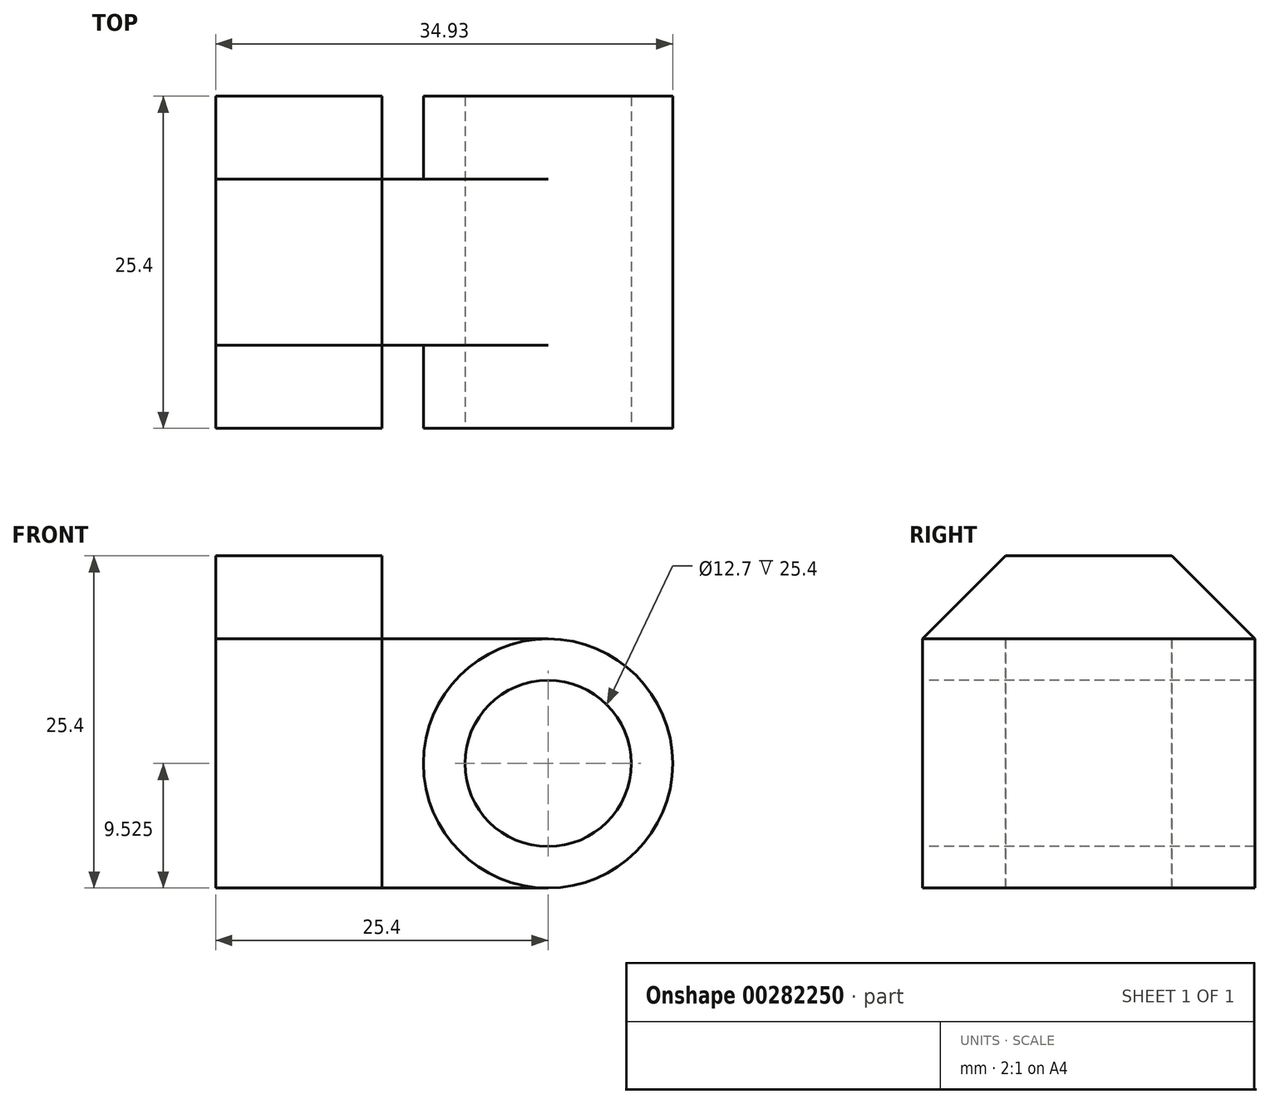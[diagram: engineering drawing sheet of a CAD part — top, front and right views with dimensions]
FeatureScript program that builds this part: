
annotation { "Feature Type Name" : "Feature", "Feature Type Description" : "" }
export const myFeature = defineFeature(function(context is Context, id is Id, definition is map)
    precondition{}
    {
        {
            var Q0;
            Q0=qCreatedBy(makeId("Right.planeOp"),FACE);
            var sketch = newSketch(context, id + "F0", { "sketchPlane" : qUnion([Q0])});
            skLineSegment(sketch, "E0.bottom", {"start": v(0, 0) * mm, "end": v(25.4, 0) * mm});
            skLineSegment(sketch, "E0.top", {"start": v(0, 25.4) * mm, "end": v(25.4, 25.4) * mm});
            skLineSegment(sketch, "E0.left", {"start": v(0, 0) * mm, "end": v(0, 25.4) * mm});
            skLineSegment(sketch, "E0.right", {"start": v(25.4, 0) * mm, "end": v(25.4, 25.4) * mm});
            skSolve(sketch);
        }
        {
            var Q0;
            Q0 = qSketchRegion(id + "F0", true);
            extrude(context, id + "F1", {"entities" : qUnion([Q0]), "depth" : 12.7 * mm});
        }
        {
            var Q0;
            Q0=qCreatedBy(makeId("Right.planeOp"),FACE);
            var sketch = newSketch(context, id + "F2", { "sketchPlane" : qUnion([Q0])});
            skLineSegment(sketch, "E1", {"start": v(0, 25.4) * mm, "end": v(0, 19.05) * mm});
            skLineSegment(sketch, "E2", {"start": v(0, 25.4) * mm, "end": v(6.35, 25.4) * mm});
            skLineSegment(sketch, "E3", {"start": v(6.35, 25.4) * mm, "end": v(0, 19.05) * mm});
            skSolve(sketch);
        }
        {
            var Q0;
            Q0 = qSketchRegion(id + "F2", true);
            extrude(context, id + "F3", {"entities" : qUnion([Q0]), "operationType" : NewBodyOperationType.REMOVE, "depth" : 12.7 * mm});
        }
        {
            var Q0;
            Q0=qCreatedBy(makeId("Right.planeOp"),FACE);
            var sketch = newSketch(context, id + "F4", { "sketchPlane" : qUnion([Q0])});
            skLineSegment(sketch, "E4", {"start": v(25.4, 19.05) * mm, "end": v(25.4, 25.4) * mm});
            skLineSegment(sketch, "E5", {"start": v(25.4, 25.4) * mm, "end": v(19.05, 25.4) * mm});
            skLineSegment(sketch, "E6", {"start": v(19.05, 25.4) * mm, "end": v(25.4, 19.05) * mm});
            skSolve(sketch);
        }
        {
            var Q0;
            Q0 = qSketchRegion(id + "F4", true);
            extrude(context, id + "F5", {"entities" : qUnion([Q0]), "operationType" : NewBodyOperationType.REMOVE, "depth" : 12.7 * mm});
        }
        {
            var Q0;
            Q0=makeQuery(id+"F1.opExtrude","CAP_FACE",FACE,{"disambiguationData":[OSD([sQuery(id+"F0.wireOp",EDGE,"E0.bottom"),sQuery(id+"F0.wireOp",EDGE,"E0.top"),sQuery(id+"F0.wireOp",EDGE,"E0.left"),sQuery(id+"F0.wireOp",EDGE,"E0.right")])],"isStart":false});
            var sketch = newSketch(context, id + "F6", { "sketchPlane" : qUnion([Q0])});
            skLineSegment(sketch, "E7.bottom", {"start": v(6.35, 19.05) * mm, "end": v(19.05, 19.05) * mm});
            skLineSegment(sketch, "E7.top", {"start": v(6.35, 0) * mm, "end": v(19.05, 0) * mm});
            skLineSegment(sketch, "E7.left", {"start": v(6.35, 19.05) * mm, "end": v(6.35, 0) * mm});
            skLineSegment(sketch, "E7.right", {"start": v(19.05, 19.05) * mm, "end": v(19.05, 0) * mm});
            skSolve(sketch);
        }
        {
            var Q0;
            Q0 = qSketchRegion(id + "F6", true);
            extrude(context, id + "F7", {"entities" : qUnion([Q0]), "operationType" : NewBodyOperationType.ADD, "depth" : 12.7 * mm});
        }
        {
            var Q0;
            Q0=qCreatedBy(makeId("Front.planeOp"),FACE);
            var sketch = newSketch(context, id + "F8", { "sketchPlane" : qUnion([Q0])});
            skCircle(sketch, "E8", {"center": v(25.4, 9.53) * mm, "radius": 9.53 * mm});
            skSolve(sketch);
        }
        {
            var Q0;
            Q0 = qSketchRegion(id + "F8", true);
            extrude(context, id + "F9", {"entities" : qUnion([Q0]), "operationType" : NewBodyOperationType.ADD, "oppositeDirection" : true, "depth" : 25.4 * mm});
        }
        {
            var Q0;
            Q0=makeQuery(id+"F9.opExtrude","CAP_FACE",FACE,{"disambiguationData":[OSD([sQuery(id+"F8.wireOp",EDGE,"E8")])],"isStart":true});
            var sketch = newSketch(context, id + "F10", { "sketchPlane" : qUnion([Q0])});
            skCircle(sketch, "E9", {"center": v(25.4, 9.53) * mm, "radius": 6.35 * mm});
            skSolve(sketch);
        }
        {
            var Q0;
            Q0 = qSketchRegion(id + "F10", true);
            extrude(context, id + "F11", {"entities" : qUnion([Q0]), "operationType" : NewBodyOperationType.REMOVE, "oppositeDirection" : true, "depth" : 25.4 * mm});
        }
    });
